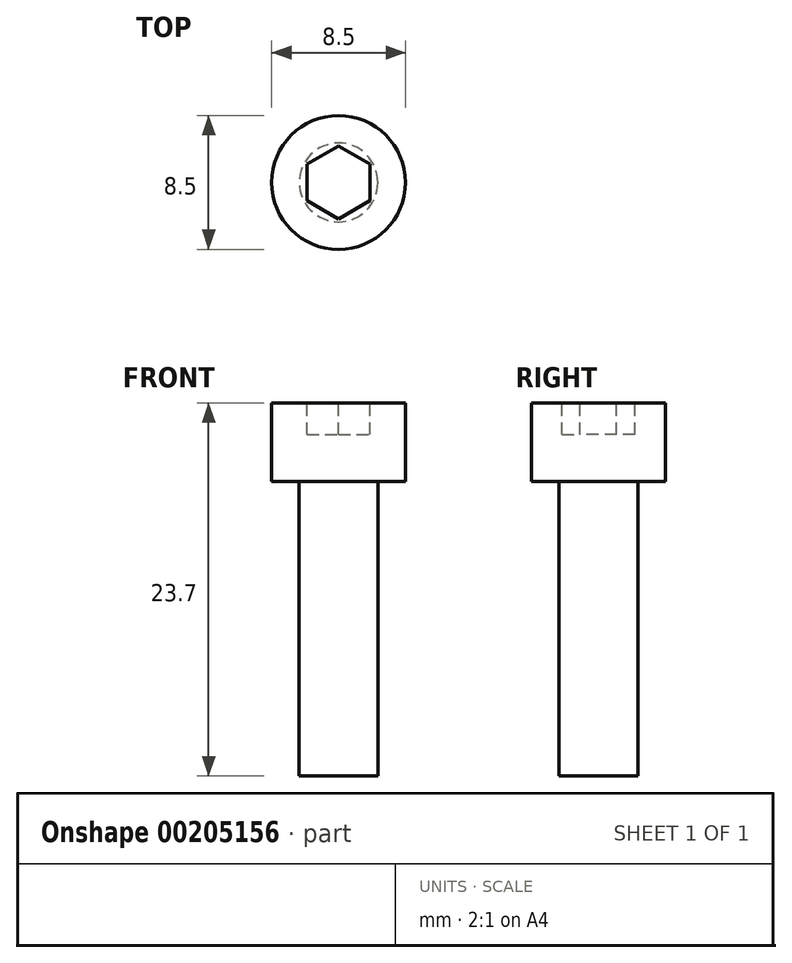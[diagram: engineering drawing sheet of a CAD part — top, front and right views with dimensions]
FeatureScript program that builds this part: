
annotation { "Feature Type Name" : "Feature", "Feature Type Description" : "" }
export const myFeature = defineFeature(function(context is Context, id is Id, definition is map)
    precondition{}
    {
        {
            var Q0;
            Q0=qCreatedBy(makeId("Top.planeOp"),FACE);
            var sketch = newSketch(context, id + "F0", { "sketchPlane" : qUnion([Q0])});
            skCircle(sketch, "E0", {"center": v(0, 0) * mm, "radius": 4.25 * mm});
            skSolve(sketch);
        }
        {
            var Q0;
            Q0=qSketchRegion(id+"F0",true);
            extrude(context, id + "F1", {"entities" : qUnion([Q0]), "depth" : 5 * mm});
        }
        {
            var Q0;
            Q0=makeQuery(id+"F1.opExtrude","CAP_FACE",FACE,{"disambiguationData":[OSD([sQuery(id+"F0.wireOp",EDGE,"E0")])],"isStart":false});
            var sketch = newSketch(context, id + "F2", { "sketchPlane" : qUnion([Q0])});
            skCircle(sketch, "E1.cCircle", {"center": v(0, 0) * mm, "radius": 2 * mm, "construction": true});
            skLineSegment(sketch, "E1.0", {"start": v(2, 1.15) * mm, "end": v(2, -1.15) * mm});
            skLineSegment(sketch, "E1.1", {"start": v(2, -1.15) * mm, "end": v(0, -2.3) * mm});
            skLineSegment(sketch, "E1.2", {"start": v(0, -2.3) * mm, "end": v(-2, -1.15) * mm});
            skLineSegment(sketch, "E1.3", {"start": v(-2, -1.15) * mm, "end": v(-2, 1.15) * mm});
            skLineSegment(sketch, "E1.4", {"start": v(-2, 1.15) * mm, "end": v(0, 2.3) * mm});
            skLineSegment(sketch, "E1.5", {"start": v(0, 2.3) * mm, "end": v(2, 1.15) * mm});
            skPoint(sketch, "E1.0.midPoint", {"position": v(2, 0) * mm});
            skSolve(sketch);
        }
        {
            var Q0;
            Q0=qSketchRegion(id+"F2",true);
            extrude(context, id + "F3", {"entities" : qUnion([Q0]), "operationType" : NewBodyOperationType.REMOVE, "oppositeDirection" : true, "depth" : 2 * mm});
        }
        {
            var Q0;
            Q0=qCreatedBy(makeId("Top.planeOp"),FACE);
            var sketch = newSketch(context, id + "F4", { "sketchPlane" : qUnion([Q0])});
            skCircle(sketch, "E2", {"center": v(0, 0) * mm, "radius": 2.5 * mm});
            skSolve(sketch);
        }
        {
            var Q0;
            Q0=qSketchRegion(id+"F4",true);
            extrude(context, id + "F5", {"entities" : qUnion([Q0]), "operationType" : NewBodyOperationType.ADD, "oppositeDirection" : true, "depth" : 40 * mm});
        }
        {
            var Q0;
            Q0=makeQuery(id+"F5.opExtrude","CAP_FACE",FACE,{"disambiguationData":[OSD([sQuery(id+"F4.wireOp",EDGE,"E2")])],"isStart":false});
            extrude(context, id + "F6", {"entities" : qUnion([Q0]), "operationType" : NewBodyOperationType.ADD, "oppositeDirection" : true, "depth" : 22.7 * mm});
        }
        {
            var Q0;
            Q0=makeQuery(id+"F5.opExtrude","CAP_FACE",FACE,{"disambiguationData":[OSD([sQuery(id+"F4.wireOp",EDGE,"E2")])],"isStart":false});
            extrude(context, id + "F7", {"entities" : qUnion([Q0]), "operationType" : NewBodyOperationType.REMOVE, "oppositeDirection" : true, "depth" : 21.3 * mm});
        }
    });
